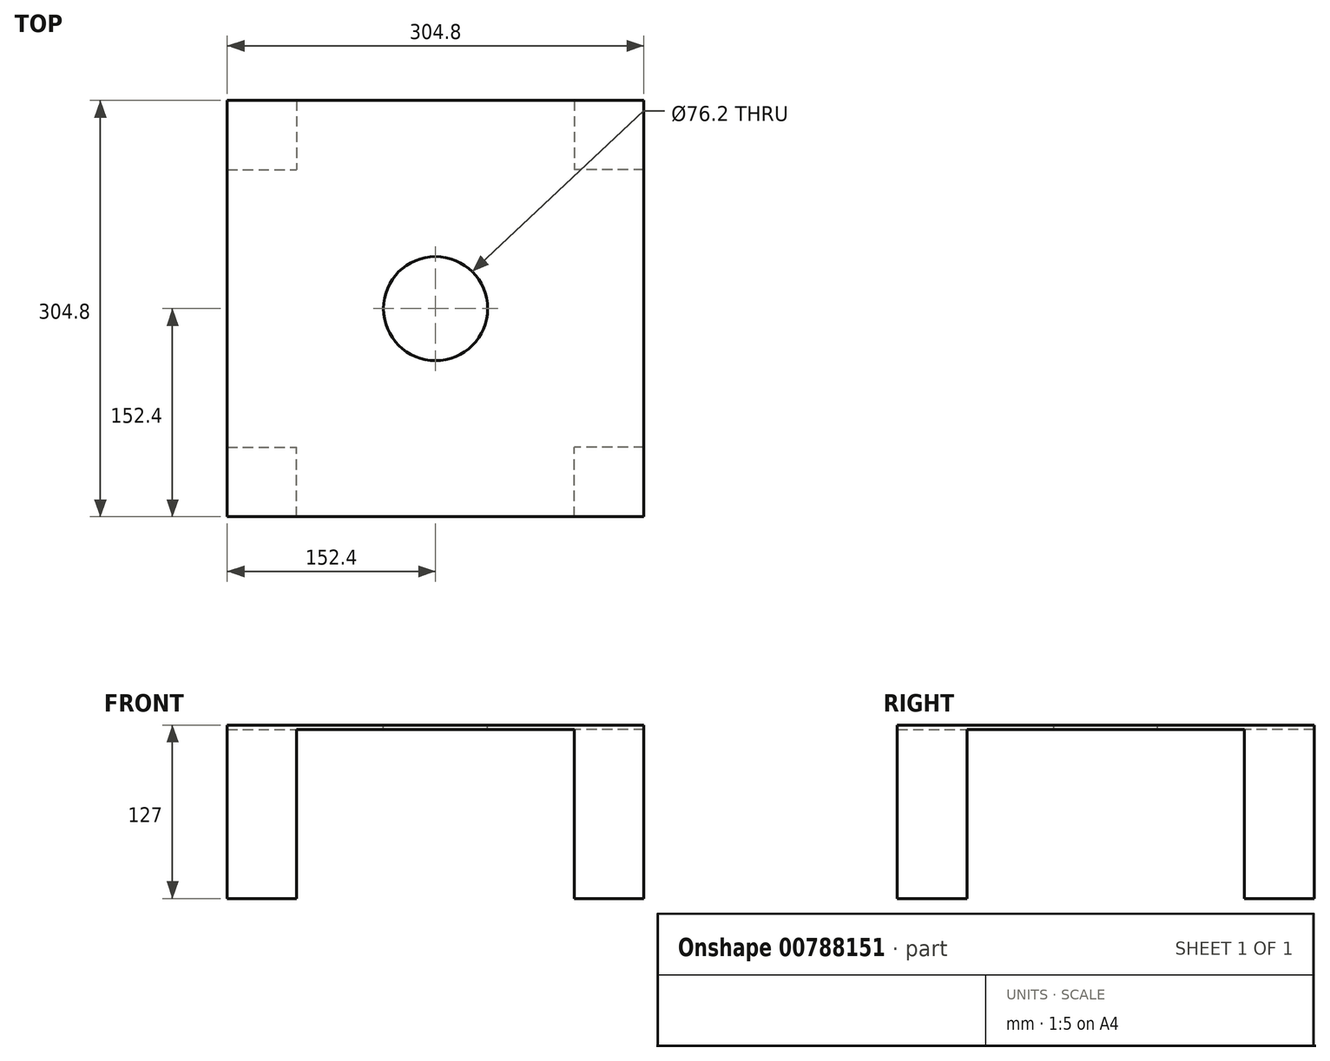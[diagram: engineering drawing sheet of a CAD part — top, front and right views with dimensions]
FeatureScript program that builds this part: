
annotation { "Feature Type Name" : "Feature", "Feature Type Description" : "" }
export const myFeature = defineFeature(function(context is Context, id is Id, definition is map)
    precondition{}
    {
        {
            var Q0;
            Q0=qCreatedBy(makeId("Top.planeOp"),FACE);
            var sketch = newSketch(context, id + "F0", { "sketchPlane" : qUnion([Q0])});
            skLineSegment(sketch, "E0.bottom", {"start": v(152.4, -152.4) * mm, "end": v(-152.4, -152.4) * mm});
            skLineSegment(sketch, "E0.top", {"start": v(152.4, 152.4) * mm, "end": v(-152.4, 152.4) * mm});
            skLineSegment(sketch, "E0.left", {"start": v(152.4, -152.4) * mm, "end": v(152.4, 152.4) * mm});
            skLineSegment(sketch, "E0.right", {"start": v(-152.4, -152.4) * mm, "end": v(-152.4, 152.4) * mm});
            skPoint(sketch, "E0.middle", {"position": v(0, 0) * mm});
            skLineSegment(sketch, "E1.bottom", {"start": v(-152.4, 152.4) * mm, "end": v(-101.6, 152.4) * mm});
            skLineSegment(sketch, "E1.top", {"start": v(-152.4, 101.6) * mm, "end": v(-101.6, 101.6) * mm});
            skLineSegment(sketch, "E1.left", {"start": v(-152.4, 152.4) * mm, "end": v(-152.4, 101.6) * mm});
            skLineSegment(sketch, "E1.right", {"start": v(-101.6, 152.4) * mm, "end": v(-101.6, 101.6) * mm});
            skLineSegment(sketch, "E2.bottom", {"start": v(152.4, 152.4) * mm, "end": v(101.6, 152.4) * mm});
            skLineSegment(sketch, "E2.top", {"start": v(152.4, 101.6) * mm, "end": v(101.6, 101.6) * mm});
            skLineSegment(sketch, "E2.left", {"start": v(152.4, 152.4) * mm, "end": v(152.4, 101.6) * mm});
            skLineSegment(sketch, "E2.right", {"start": v(101.6, 152.4) * mm, "end": v(101.6, 101.6) * mm});
            skLineSegment(sketch, "E3.bottom", {"start": v(-152.4, -152.4) * mm, "end": v(-101.6, -152.4) * mm});
            skLineSegment(sketch, "E3.top", {"start": v(-152.4, -101.6) * mm, "end": v(-101.6, -101.6) * mm});
            skLineSegment(sketch, "E3.left", {"start": v(-152.4, -152.4) * mm, "end": v(-152.4, -101.6) * mm});
            skLineSegment(sketch, "E3.right", {"start": v(-101.6, -152.4) * mm, "end": v(-101.6, -101.6) * mm});
            skLineSegment(sketch, "E4.bottom", {"start": v(152.4, -152.4) * mm, "end": v(101.6, -152.4) * mm});
            skLineSegment(sketch, "E4.top", {"start": v(152.4, -101.6) * mm, "end": v(101.6, -101.6) * mm});
            skLineSegment(sketch, "E4.left", {"start": v(152.4, -152.4) * mm, "end": v(152.4, -101.6) * mm});
            skLineSegment(sketch, "E4.right", {"start": v(101.6, -152.4) * mm, "end": v(101.6, -101.6) * mm});
            skCircle(sketch, "E5", {"center": v(0, 0) * mm, "radius": 38.1 * mm});
            skSolve(sketch);
        }
        {
            var Q0;
            {var subQ3=sQuery(id+"F0.wireOp",EDGE,"E1.top");Q0=makeQuery(id+"F0.imprint","IMPRINT",FACE,{"disambiguationData":[TD([[makeQuery(id+"F0.imprint","IMPRINT",EDGE,{"derivedFrom":subQ3}),-1.0]])]});}
            extrude(context, id + "F1", {"entities" : qUnion([Q0]), "oppositeDirection" : true, "depth" : 3.17 * mm, "offsetDistance" : 25.4 * mm});
        }
        {
            var Q0;
            {var subQ4=sQuery(id+"F0.wireOp",EDGE,"E3.top");Q0=makeQuery(id+"F0.imprint","IMPRINT",FACE,{"disambiguationData":[TD([[makeQuery(id+"F0.imprint","IMPRINT",EDGE,{"derivedFrom":subQ4}),-1.0]])]});}
            var Q1;
            {var subQ4=sQuery(id+"F0.wireOp",EDGE,"E1.top");Q1=makeQuery(id+"F0.imprint","IMPRINT",FACE,{"disambiguationData":[TD([[makeQuery(id+"F0.imprint","IMPRINT",EDGE,{"derivedFrom":subQ4}),1.0]])]});}
            var Q2;
            {var subQ4=sQuery(id+"F0.wireOp",EDGE,"E2.top");Q2=makeQuery(id+"F0.imprint","IMPRINT",FACE,{"disambiguationData":[TD([[makeQuery(id+"F0.imprint","IMPRINT",EDGE,{"derivedFrom":subQ4}),-1.0]])]});}
            var Q3;
            {var subQ4=sQuery(id+"F0.wireOp",EDGE,"E4.top");Q3=makeQuery(id+"F0.imprint","IMPRINT",FACE,{"disambiguationData":[TD([[makeQuery(id+"F0.imprint","IMPRINT",EDGE,{"derivedFrom":subQ4}),1.0]])]});}
            extrude(context, id + "F2", {"entities" : qUnion([Q0, Q1, Q2, Q3]), "operationType" : NewBodyOperationType.ADD, "oppositeDirection" : true, "depth" : 127 * mm, "offsetDistance" : 25.4 * mm});
        }
    });
